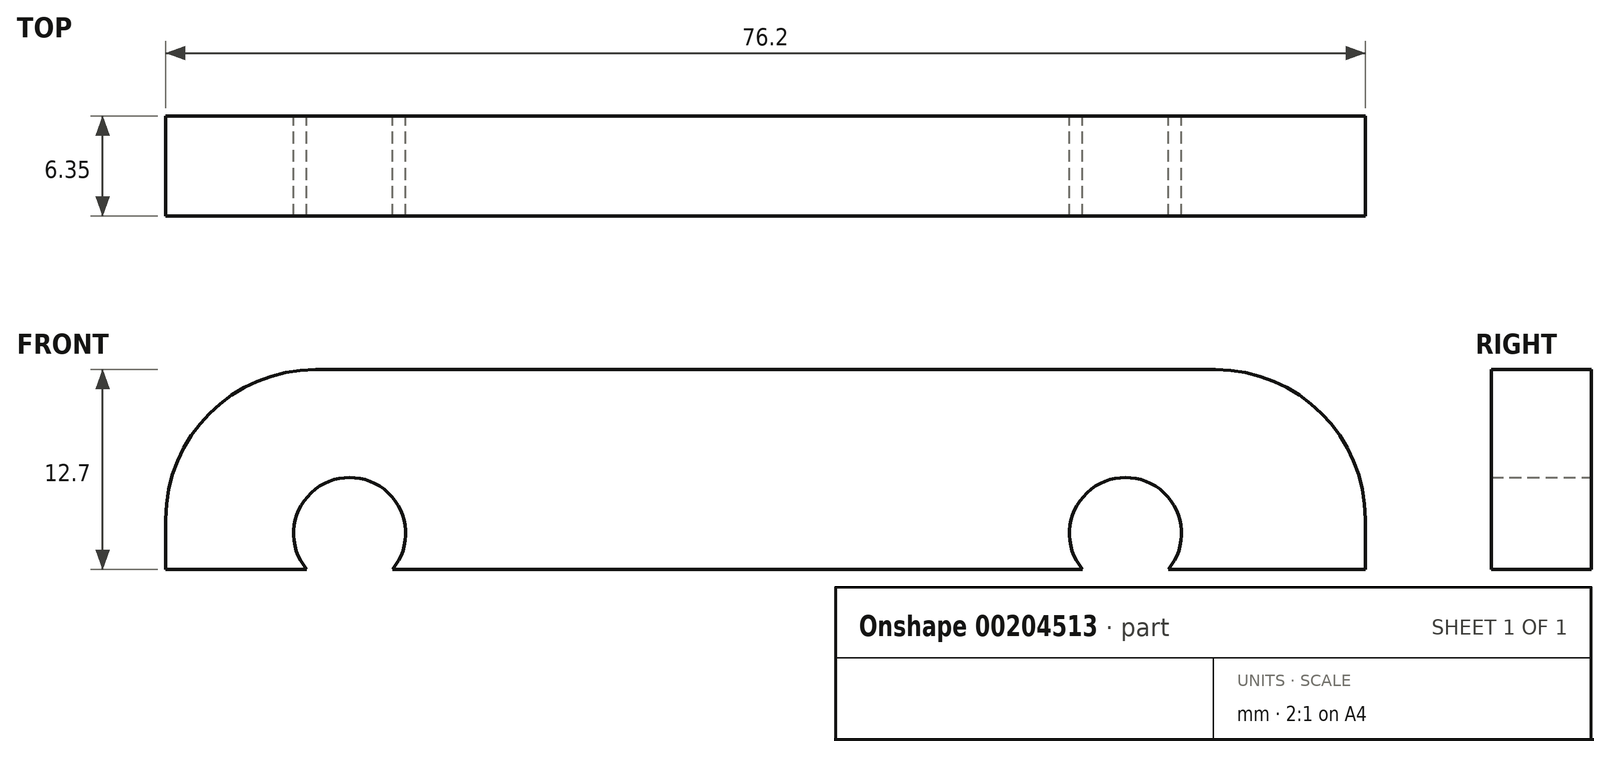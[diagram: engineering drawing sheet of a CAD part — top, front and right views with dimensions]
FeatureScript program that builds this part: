
annotation { "Feature Type Name" : "Feature", "Feature Type Description" : "" }
export const myFeature = defineFeature(function(context is Context, id is Id, definition is map)
    precondition{}
    {
        {
            var Q0;
            Q0=qCreatedBy(makeId("Front.planeOp"),FACE);
            var sketch = newSketch(context, id + "F0", { "sketchPlane" : qUnion([Q0])});
            skLineSegment(sketch, "E0.bottom", {"start": v(38.1, -6.35) * mm, "end": v(25.58, -6.35) * mm});
            skLineSegment(sketch, "E0.top", {"start": v(38.1, 6.35) * mm, "end": v(-38.1, 6.35) * mm});
            skLineSegment(sketch, "E0.left", {"start": v(38.1, -6.35) * mm, "end": v(38.1, 6.35) * mm});
            skLineSegment(sketch, "E0.right", {"start": v(-38.1, -6.35) * mm, "end": v(-38.1, 6.35) * mm});
            skArc(sketch, "E1", {"start": v(-23.7, -6.35) * mm, "mid": v(-26.42, -0.5) * mm, "end": v(-29.14, -6.35) * mm});
            skArc(sketch, "E2", {"start": v(25.58, -6.35) * mm, "mid": v(22.86, -0.5) * mm, "end": v(20.14, -6.35) * mm});
            skLineSegment(sketch, "E3.trimOffspring", {"start": v(20.14, -6.35) * mm, "end": v(-23.7, -6.35) * mm});
            skLineSegment(sketch, "E4.trimOffspring", {"start": v(-29.14, -6.35) * mm, "end": v(-38.1, -6.35) * mm});
            skSolve(sketch);
        }
        {
            var Q0;
            Q0 = qSketchRegion(id + "F0", true);
            extrude(context, id + "F1", {"entities" : qUnion([Q0]), "depth" : 6.35 * mm});
        }
        {
            var Q0;
            Q0=makeQuery(id+"F1.opExtrude","SWEPT_EDGE",EDGE,{"disambiguationData":[OSD([sQuery(id+"F0.wireOp",EDGE,"E0.top"),sQuery(id+"F0.wireOp",EDGE,"E0.right")])]});
            var Q1;
            Q1=makeQuery(id+"F1.opExtrude","SWEPT_EDGE",EDGE,{"disambiguationData":[OSD([sQuery(id+"F0.wireOp",EDGE,"E0.top"),sQuery(id+"F0.wireOp",EDGE,"E0.left")])]});
            fillet(context, id + "F2", {"entities" : qUnion([Q0, Q1]), "radius" : 9.52 * mm, "tangentPropagation" : true, "allowEdgeOverflow" : false});
        }
    });
